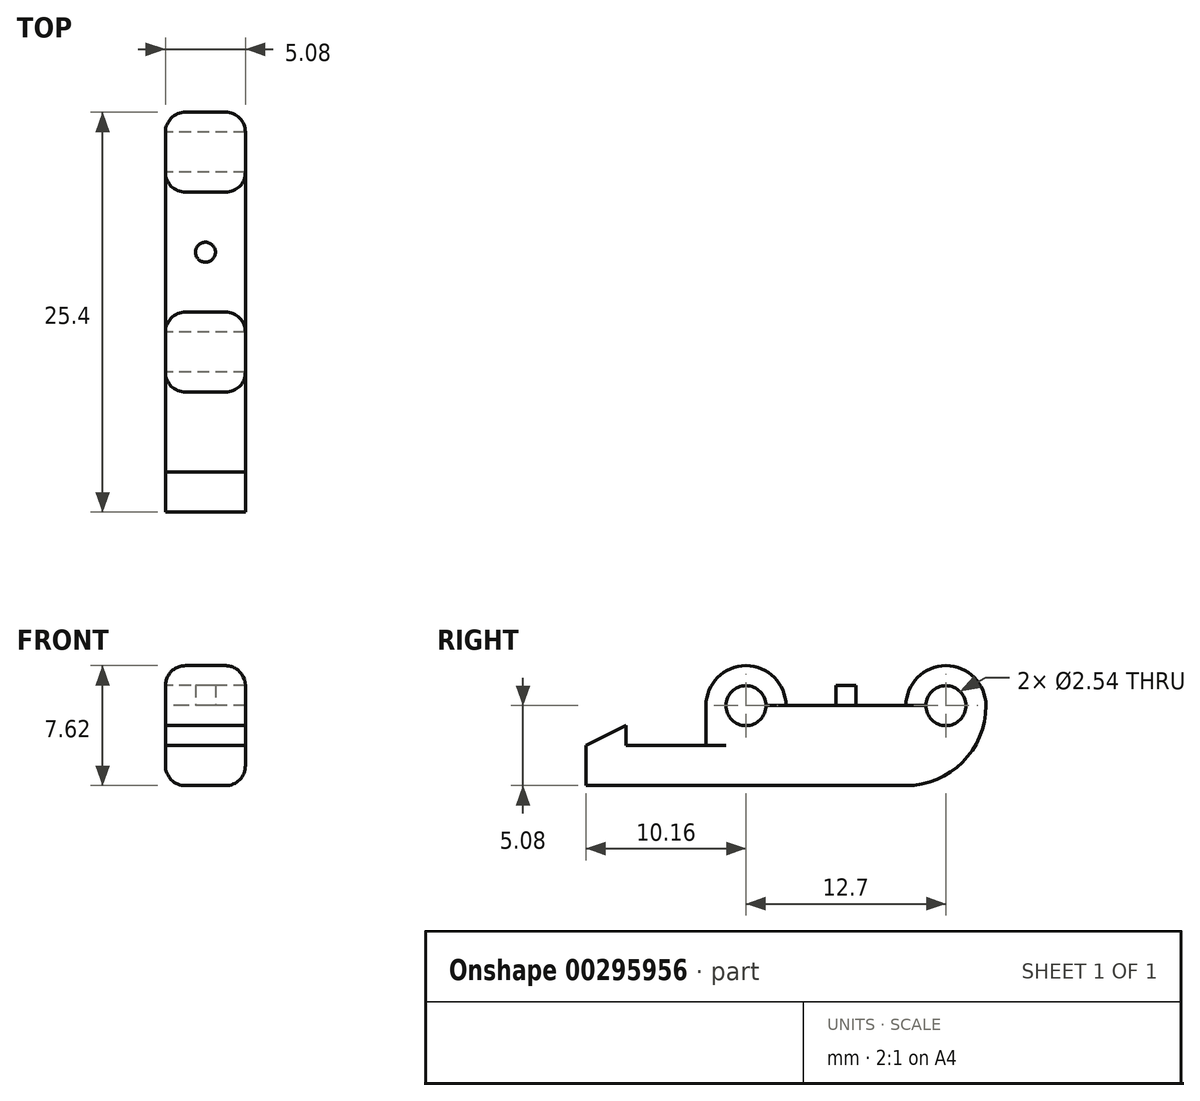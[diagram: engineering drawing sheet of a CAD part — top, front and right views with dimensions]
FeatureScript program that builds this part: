
annotation { "Feature Type Name" : "Feature", "Feature Type Description" : "" }
export const myFeature = defineFeature(function(context is Context, id is Id, definition is map)
    precondition{}
    {
        {
            var Q0;
            Q0=qCreatedBy(makeId("Right.planeOp"),FACE);
            var sketch = newSketch(context, id + "F0", { "sketchPlane" : qUnion([Q0])});
            skCircle(sketch, "E0", {"center": v(0, 0) * mm, "radius": 2.54 * mm});
            skCircle(sketch, "E1", {"center": v(0, 0) * mm, "radius": 1.27 * mm});
            skLineSegment(sketch, "E2", {"start": v(-2.54, 0) * mm, "end": v(-2.54, -5.08) * mm});
            skLineSegment(sketch, "E3", {"start": v(-2.54, -5.08) * mm, "end": v(15.24, -5.08) * mm});
            skLineSegment(sketch, "E4", {"start": v(15.24, -5.08) * mm, "end": v(15.24, 0) * mm});
            skCircle(sketch, "E5", {"center": v(12.7, 0) * mm, "radius": 2.54 * mm});
            skCircle(sketch, "E6", {"center": v(12.7, 0) * mm, "radius": 1.27 * mm});
            skLineSegment(sketch, "E7", {"start": v(10.16, 0) * mm, "end": v(10.16, 0) * mm});
            skLineSegment(sketch, "E8", {"start": v(2.54, 0) * mm, "end": v(2.54, 0) * mm});
            skLineSegment(sketch, "E9", {"start": v(2.54, 0) * mm, "end": v(10.16, 0) * mm});
            skLineSegment(sketch, "E10", {"start": v(-2.54, -5.08) * mm, "end": v(-10.16, -5.08) * mm});
            skLineSegment(sketch, "E11", {"start": v(-10.16, -5.08) * mm, "end": v(-10.16, -2.54) * mm});
            skLineSegment(sketch, "E12", {"start": v(-10.16, -2.54) * mm, "end": v(-2.54, -2.54) * mm});
            skLineSegment(sketch, "E13", {"start": v(-10.16, -2.54) * mm, "end": v(-7.62, -1.27) * mm});
            skLineSegment(sketch, "E14", {"start": v(-7.62, -1.27) * mm, "end": v(-7.62, -2.54) * mm});
            skSolve(sketch);
        }
        {
            var Q0;
            Q0 = qSketchRegion(id + "F0", true);
            extrude(context, id + "F1", {"entities" : qUnion([Q0]), "depth" : 5.08 * mm});
        }
        {
            var Q0;
            Q0=makeQuery(id+"F1.opExtrude","SWEPT_FACE",FACE,{"disambiguationData":[OSD([sQuery(id+"F0.wireOp",EDGE,"E9")])]});
            var sketch = newSketch(context, id + "F2", { "sketchPlane" : qUnion([Q0])});
            skCircle(sketch, "E15", {"center": v(2.54, 6.35) * mm, "radius": 0.64 * mm});
            skPoint(sketch, "E15.centerSnap0", {"position": v(0, 6.35) * mm});
            skSolve(sketch);
        }
        {
            var Q0;
            Q0 = qSketchRegion(id + "F2", true);
            extrude(context, id + "F3", {"entities" : qUnion([Q0]), "operationType" : NewBodyOperationType.ADD, "depth" : 1.27 * mm});
        }
        {
            var Q0;
            Q0=makeQuery(id+"F1.opExtrude","SWEPT_EDGE",EDGE,{"disambiguationData":[OSD([sQuery(id+"F0.wireOp",EDGE,"E3"),sQuery(id+"F0.wireOp",EDGE,"E4"),sQuery(id+"F0.wireOp",EDGE,"c4793016-eede-48da-aba7-3a384f1f3df9")])]});
            fillet(context, id + "F4", {"entities" : qUnion([Q0]), "radius" : 5.08 * mm, "tangentPropagation" : true, "allowEdgeOverflow" : false});
        }
        {
            var Q0;
            {var subQ0=sQuery(id+"F0.wireOp",EDGE,"E4");var subQ1=sQuery(id+"F0.wireOp",EDGE,"E3");Q0=makeQuery(id+"F4.opFillet","BLEND_EDGE",EDGE,{"blendedFrom":[makeQuery(id+"F1.opExtrude","SWEPT_EDGE",EDGE,{"disambiguationData":[OSD([subQ1,subQ0])]}),makeQuery(id+"F1.opExtrude","CAP_FACE",FACE,{"disambiguationData":[OSD([sQuery(id+"F0.wireOp",EDGE,"E0"),sQuery(id+"F0.wireOp",EDGE,"E1"),sQuery(id+"F0.wireOp",EDGE,"E2"),subQ1,subQ0,sQuery(id+"F0.wireOp",EDGE,"E5"),sQuery(id+"F0.wireOp",EDGE,"E6"),sQuery(id+"F0.wireOp",EDGE,"E9"),sQuery(id+"F0.wireOp",EDGE,"E10"),sQuery(id+"F0.wireOp",EDGE,"E11"),sQuery(id+"F0.wireOp",EDGE,"E12"),sQuery(id+"F0.wireOp",EDGE,"E13"),sQuery(id+"F0.wireOp",EDGE,"E14")])],"isStart":false})],"blendedInto":[makeQuery(id+"F1.opExtrude","CAP_FACE",FACE,{"disambiguationData":[OSD([sQuery(id+"F0.wireOp",EDGE,"E0"),sQuery(id+"F0.wireOp",EDGE,"E1"),sQuery(id+"F0.wireOp",EDGE,"E2"),subQ1,subQ0,sQuery(id+"F0.wireOp",EDGE,"E5"),sQuery(id+"F0.wireOp",EDGE,"E6"),sQuery(id+"F0.wireOp",EDGE,"E9"),sQuery(id+"F0.wireOp",EDGE,"E10"),sQuery(id+"F0.wireOp",EDGE,"E11"),sQuery(id+"F0.wireOp",EDGE,"E12"),sQuery(id+"F0.wireOp",EDGE,"E13"),sQuery(id+"F0.wireOp",EDGE,"E14")])],"isStart":false})]});}
            var Q1;
            {var subQ0=sQuery(id+"F0.wireOp",EDGE,"E4");var subQ1=sQuery(id+"F0.wireOp",EDGE,"E3");Q1=makeQuery(id+"F4.opFillet","BLEND_EDGE",EDGE,{"blendedFrom":[makeQuery(id+"F1.opExtrude","SWEPT_EDGE",EDGE,{"disambiguationData":[OSD([subQ1,subQ0])]}),makeQuery(id+"F1.opExtrude","CAP_FACE",FACE,{"disambiguationData":[OSD([sQuery(id+"F0.wireOp",EDGE,"E0"),sQuery(id+"F0.wireOp",EDGE,"E1"),sQuery(id+"F0.wireOp",EDGE,"E2"),subQ1,subQ0,sQuery(id+"F0.wireOp",EDGE,"E5"),sQuery(id+"F0.wireOp",EDGE,"E6"),sQuery(id+"F0.wireOp",EDGE,"E9"),sQuery(id+"F0.wireOp",EDGE,"E10"),sQuery(id+"F0.wireOp",EDGE,"E11"),sQuery(id+"F0.wireOp",EDGE,"E12"),sQuery(id+"F0.wireOp",EDGE,"E13"),sQuery(id+"F0.wireOp",EDGE,"E14")])],"isStart":true})],"blendedInto":[makeQuery(id+"F1.opExtrude","CAP_FACE",FACE,{"disambiguationData":[OSD([sQuery(id+"F0.wireOp",EDGE,"E0"),sQuery(id+"F0.wireOp",EDGE,"E1"),sQuery(id+"F0.wireOp",EDGE,"E2"),subQ1,subQ0,sQuery(id+"F0.wireOp",EDGE,"E5"),sQuery(id+"F0.wireOp",EDGE,"E6"),sQuery(id+"F0.wireOp",EDGE,"E9"),sQuery(id+"F0.wireOp",EDGE,"E10"),sQuery(id+"F0.wireOp",EDGE,"E11"),sQuery(id+"F0.wireOp",EDGE,"E12"),sQuery(id+"F0.wireOp",EDGE,"E13"),sQuery(id+"F0.wireOp",EDGE,"E14")])],"isStart":true})]});}
            var Q2;
            Q2=makeQuery(id+"F1.opExtrude","CAP_EDGE",EDGE,{"disambiguationData":[OSD([sQuery(id+"F0.wireOp",EDGE,"E0")])],"isStart":false});
            var Q3;
            Q3=makeQuery(id+"F1.opExtrude","CAP_EDGE",EDGE,{"disambiguationData":[OSD([sQuery(id+"F0.wireOp",EDGE,"E0")])],"isStart":true});
            fillet(context, id + "F5", {"entities" : qUnion([Q0, Q1, Q2, Q3]), "radius" : 1.27 * mm, "tangentPropagation" : true, "allowEdgeOverflow" : false});
        }
    });
